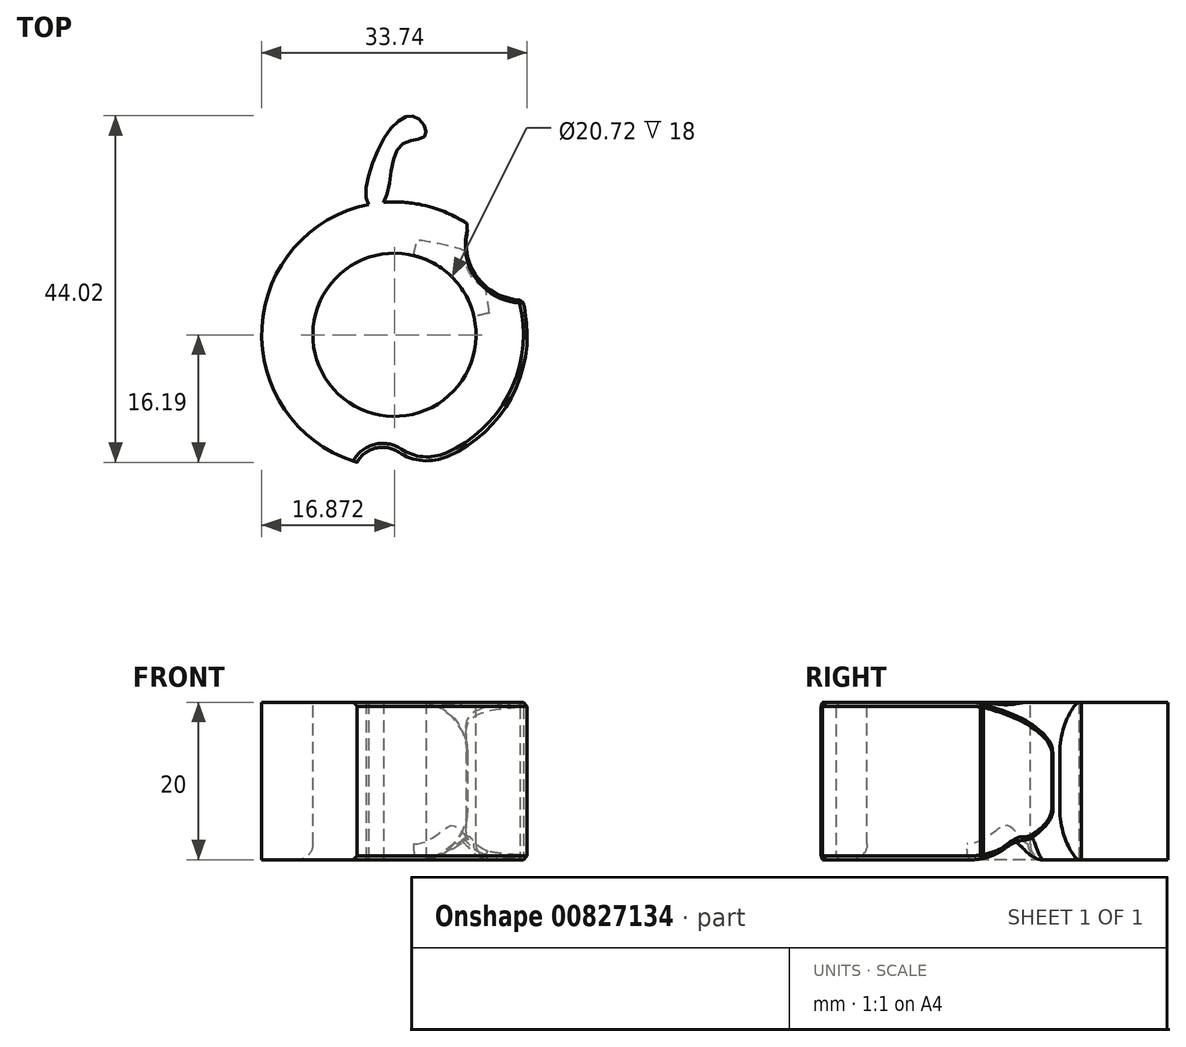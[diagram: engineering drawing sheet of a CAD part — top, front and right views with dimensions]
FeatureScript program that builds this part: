
annotation { "Feature Type Name" : "Feature", "Feature Type Description" : "" }
export const myFeature = defineFeature(function(context is Context, id is Id, definition is map)
    precondition{}
    {
        {
            var Q0;
            Q0=qCreatedBy(makeId("Top.planeOp"),FACE);
            var sketch = newSketch(context, id + "F0", { "sketchPlane" : qUnion([Q0])});
            skArc(sketch, "E0", {"start": v(0, 19.96) * mm, "mid": v(5.66, -13.29) * mm, "end": v(1.94, 20.24) * mm});
            skFitSpline(sketch, "E1", {"points": [v(1.94, 20.24) * mm, v(4, 27.35) * mm, v(7.23, 28.75) * mm, v(5.97, 31.13) * mm, v(1.94, 28.26) * mm, v(0, 19.96) * mm, v(1.94, 20.24) * mm]});
            skCircle(sketch, "E2", {"center": v(1.8, -14.57) * mm, "radius": 3.7 * mm});
            skCircle(sketch, "E3", {"center": v(17.22, 17.2) * mm, "radius": 4.68 * mm});
            skCircle(sketch, "E4", {"center": v(19.61, 15.04) * mm, "radius": 7.2 * mm});
            skSolve(sketch);
        }
        {
            var Q0;
            {var subQ0=sQuery(id+"F0.wireOp",EDGE,"E1");var subQ1=sQuery(id+"F0.wireOp",EDGE,"E0");var subQ2=makeQuery(id+"F0.imprint","INTERSECT",VERTEX,{"disambiguationData":[OD(0.0)],"derivedFrom":[subQ1,subQ0]});Q0=makeQuery(id+"F0.imprint","IMPRINT",FACE,{"disambiguationData":[TD([[makeQuery(id+"F0.imprint","IMPRINT",EDGE,{"disambiguationData":[TD([[subQ2,1.0]])],"derivedFrom":subQ0}),1.0]])]});}
            var Q1;
            {var subQ0=sQuery(id+"F0.wireOp",EDGE,"E0");Q1=makeQuery(id+"F0.imprint","IMPRINT",FACE,{"disambiguationData":[TD([[makeQuery(id+"F0.imprint","IMPRINT",EDGE,{"derivedFrom":subQ0}),1.0]])]});}
            extrude(context, id + "F1", {"entities" : qUnion([Q0, Q1]), "depth" : 20 * mm, "offsetDistance" : 25 * mm});
        }
        {
            var Q0;
            Q0=makeQuery(id+"F1.opExtrude","CAP_FACE",FACE,{"disambiguationData":[OSD([sQuery(id+"F0.wireOp",EDGE,"E0"),sQuery(id+"F0.wireOp",EDGE,"E1")])],"isStart":false});
            var sketch = newSketch(context, id + "F2", { "sketchPlane" : qUnion([Q0])});
            skCircle(sketch, "E5", {"center": v(3.31, 3.42) * mm, "radius": 10.36 * mm});
            skSolve(sketch);
        }
        {
            var Q0;
            Q0=makeQuery(id+"F2.imprint","IMPRINT",FACE,{"disambiguationData":[TD([[makeQuery(id+"F2.imprint","IMPRINT",EDGE,{"derivedFrom":sQuery(id+"F2.wireOp",EDGE,"E5")}),1.0]])]});
            extrude(context, id + "F3", {"entities" : qUnion([Q0]), "operationType" : NewBodyOperationType.REMOVE, "oppositeDirection" : true, "depth" : 25 * mm, "offsetDistance" : 25 * mm});
        }
        {
            var Q0;
            {var subQ0=sQuery(id+"F0.wireOp",EDGE,"E2");var subQ1=sQuery(id+"F0.wireOp",EDGE,"E0");Q0=makeQuery(id+"F1.opExtrude","SWEPT_EDGE",EDGE,{"disambiguationData":[OSD([subQ1,subQ0]),TDD([makeQuery(id+"F0.imprint","INTERSECT",VERTEX,{"disambiguationData":[OD(1.0)],"derivedFrom":[subQ1,subQ0]})])]});}
            var Q1;
            Q1=makeQuery(id+"F1.opExtrude","CAP_EDGE",EDGE,{"disambiguationData":[OSD([sQuery(id+"F0.wireOp",EDGE,"E3")])],"isStart":true});
            var Q2;
            Q2=makeQuery(id+"F1.opExtrude","CAP_EDGE",EDGE,{"disambiguationData":[OSD([sQuery(id+"F0.wireOp",EDGE,"E3")])],"isStart":false});
            fillet(context, id + "F4", {"entities" : qUnion([Q0, Q1, Q2]), "radius" : 6.5 * mm, "tangentPropagation" : true, "allowEdgeOverflow" : false});
        }
        {
            var Q0;
            Q0=makeQuery(id+"F3.boolean.opBoolean","COPY",EDGE,{"derivedFrom":makeQuery(id+"F3.opExtrude","CAP_EDGE",EDGE,{"disambiguationData":[OSD([sQuery(id+"F2.wireOp",EDGE,"E5")])],"isStart":true})});
            var Q1;
            Q1=makeQuery(id+"F3.boolean.opBoolean","INTERSECT",EDGE,{"derivedFrom":[makeQuery(id+"F1.opExtrude","CAP_FACE",FACE,{"disambiguationData":[OSD([sQuery(id+"F0.wireOp",EDGE,"E0"),sQuery(id+"F0.wireOp",EDGE,"E1"),sQuery(id+"F0.wireOp",EDGE,"E2"),sQuery(id+"F0.wireOp",EDGE,"E3"),sQuery(id+"F0.wireOp",EDGE,"E4")])],"isStart":true}),makeQuery(id+"F3.opExtrude","SWEPT_FACE",FACE,{"disambiguationData":[OSD([sQuery(id+"F2.wireOp",EDGE,"E5")])]})]});
            fillet(context, id + "F5", {"entities" : qUnion([Q0, Q1]), "radius" : 2 * mm, "tangentPropagation" : true, "allowEdgeOverflow" : false});
        }
        {
            var Q0;
            {var subQ0=sQuery(id+"F0.wireOp",EDGE,"E0");Q0=makeQuery(id+"F1.opExtrude","CAP_EDGE",EDGE,{"disambiguationData":[OSD([subQ0]),TDD([makeQuery(id+"F0.imprint","IMPRINT",EDGE,{"disambiguationData":[TD([[makeQuery(id+"F0.imprint","INTERSECT",VERTEX,{"disambiguationData":[OD(1.0)],"derivedFrom":[subQ0,sQuery(id+"F0.wireOp",EDGE,"E2")]}),-1.0]])],"derivedFrom":subQ0})])],"isStart":false});}
            var Q1;
            {var subQ0=sQuery(id+"F0.wireOp",EDGE,"E0");Q1=makeQuery(id+"F1.opExtrude","CAP_EDGE",EDGE,{"disambiguationData":[OSD([subQ0]),TDD([makeQuery(id+"F0.imprint","IMPRINT",EDGE,{"disambiguationData":[TD([[makeQuery(id+"F0.imprint","INTERSECT",VERTEX,{"disambiguationData":[OD(0.0)],"derivedFrom":[subQ0,sQuery(id+"F0.wireOp",EDGE,"E1")]}),-1.0]])],"derivedFrom":subQ0})])],"isStart":false});}
            var Q2;
            Q2=makeQuery(id+"F1.opExtrude","SWEPT_EDGE",EDGE,{"disambiguationData":[OSD([sQuery(id+"F0.wireOp",EDGE,"E0"),sQuery(id+"F0.wireOp",EDGE,"E4")])]});
            var Q3;
            {var subQ0=sQuery(id+"F0.wireOp",EDGE,"E0");Q3=makeQuery(id+"F1.opExtrude","CAP_EDGE",EDGE,{"disambiguationData":[OSD([subQ0]),TDD([makeQuery(id+"F0.imprint","IMPRINT",EDGE,{"disambiguationData":[TD([[makeQuery(id+"F0.imprint","INTERSECT",VERTEX,{"disambiguationData":[OD(1.0)],"derivedFrom":[subQ0,sQuery(id+"F0.wireOp",EDGE,"E1")]}),1.0]])],"derivedFrom":subQ0})])],"isStart":false});}
            var Q4;
            {var subQ0=sQuery(id+"F0.wireOp",EDGE,"E0");Q4=makeQuery(id+"F1.opExtrude","CAP_EDGE",EDGE,{"disambiguationData":[OSD([subQ0]),TDD([makeQuery(id+"F0.imprint","IMPRINT",EDGE,{"disambiguationData":[TD([[makeQuery(id+"F0.imprint","INTERSECT",VERTEX,{"disambiguationData":[OD(0.0)],"derivedFrom":[subQ0,sQuery(id+"F0.wireOp",EDGE,"E1")]}),-1.0]])],"derivedFrom":subQ0})])],"isStart":true});}
            var Q5;
            Q5=makeQuery(id+"F1.opExtrude","CAP_EDGE",EDGE,{"disambiguationData":[OSD([sQuery(id+"F0.wireOp",EDGE,"E2")])],"isStart":true});
            var Q6;
            Q6=makeQuery(id+"F4.opFillet","BLEND_EDGE",EDGE,{"blendedFrom":[makeQuery(id+"F1.opExtrude","CAP_EDGE",EDGE,{"disambiguationData":[OSD([sQuery(id+"F0.wireOp",EDGE,"E3")])],"isStart":true}),makeQuery(id+"F1.opExtrude","SWEPT_FACE",FACE,{"disambiguationData":[OSD([sQuery(id+"F0.wireOp",EDGE,"E4")])]})],"blendedInto":[makeQuery(id+"F1.opExtrude","SWEPT_FACE",FACE,{"disambiguationData":[OSD([sQuery(id+"F0.wireOp",EDGE,"E4")])]})]});
            chamfer(context, id + "F6", {"entities" : qUnion([Q0, Q1, Q2, Q3, Q4, Q5, Q6]), "width" : .5 * mm, "tangentPropagation" : true});
        }
    });
